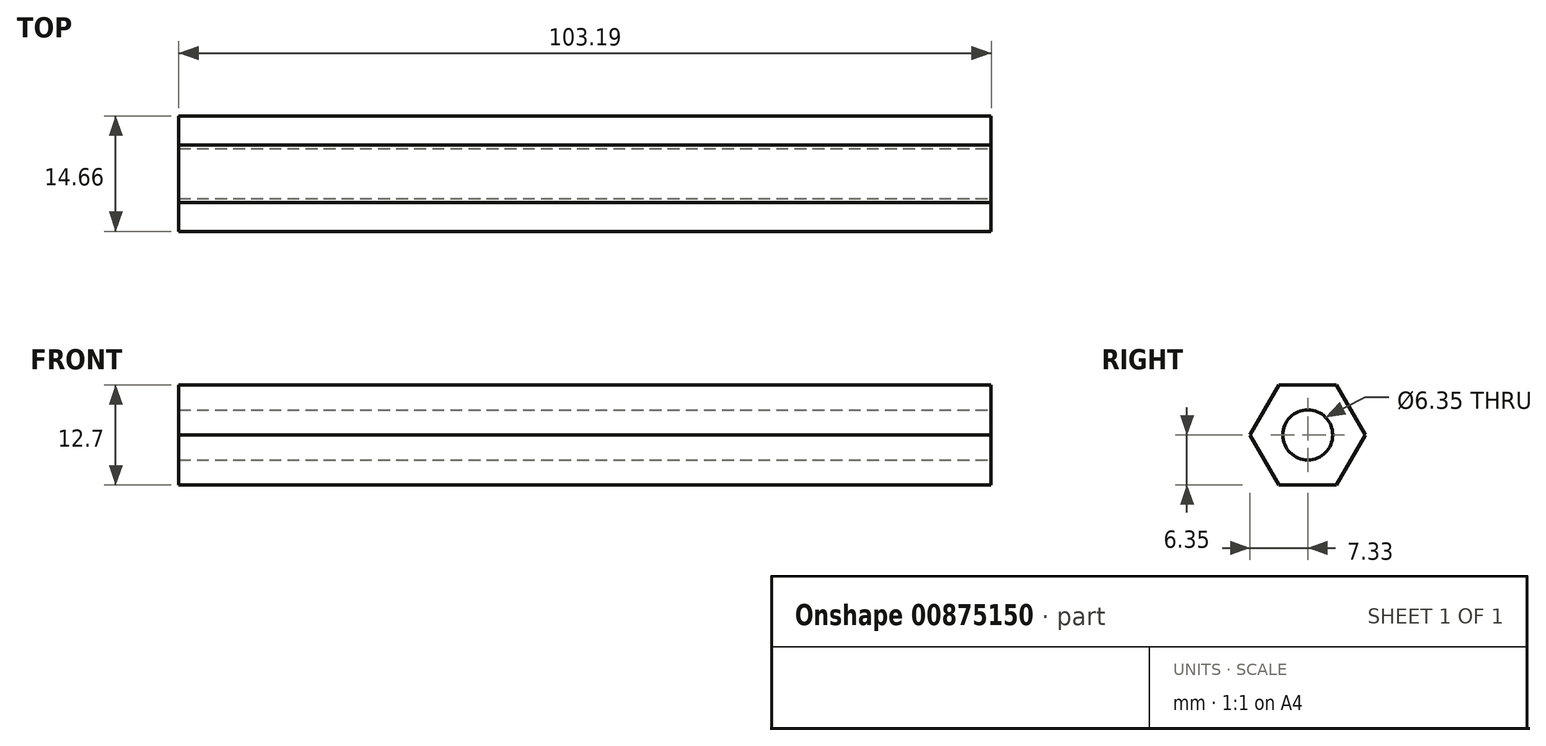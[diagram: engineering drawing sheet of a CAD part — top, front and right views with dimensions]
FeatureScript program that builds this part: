
annotation { "Feature Type Name" : "Feature", "Feature Type Description" : "" }
export const myFeature = defineFeature(function(context is Context, id is Id, definition is map)
    precondition{}
    {
        {
            var Q0;
            Q0=qCreatedBy(makeId("Right.planeOp"),FACE);
            var sketch = newSketch(context, id + "F0", { "sketchPlane" : qUnion([Q0])});
            skCircle(sketch, "E0.cCircle", {"center": v(0, 0) * mm, "radius": 6.35 * mm, "construction": true});
            skLineSegment(sketch, "E0.0", {"start": v(-3.67, 6.35) * mm, "end": v(3.67, 6.35) * mm});
            skLineSegment(sketch, "E0.1", {"start": v(3.67, 6.35) * mm, "end": v(7.33, 0) * mm});
            skLineSegment(sketch, "E0.2", {"start": v(7.33, 0) * mm, "end": v(3.67, -6.35) * mm});
            skLineSegment(sketch, "E0.3", {"start": v(3.67, -6.35) * mm, "end": v(-3.67, -6.35) * mm});
            skLineSegment(sketch, "E0.4", {"start": v(-3.67, -6.35) * mm, "end": v(-7.33, 0) * mm});
            skLineSegment(sketch, "E0.5", {"start": v(-7.33, 0) * mm, "end": v(-3.67, 6.35) * mm});
            skPoint(sketch, "E0.0.midPoint", {"position": v(0, 6.35) * mm});
            skSolve(sketch);
        }
        {
            var Q0;
            Q0 = qSketchRegion(id + "F0", true);
            extrude(context, id + "F1", {"entities" : qUnion([Q0]), "depth" : 103.19 * mm, "offsetDistance" : 25.4 * mm});
        }
        {
            var Q0;
            Q0=makeQuery(id+"F1.opExtrude","CAP_FACE",FACE,{"disambiguationData":[OSD([sQuery(id+"F0.wireOp",EDGE,"E0.0"),sQuery(id+"F0.wireOp",EDGE,"E0.1"),sQuery(id+"F0.wireOp",EDGE,"E0.2"),sQuery(id+"F0.wireOp",EDGE,"E0.3"),sQuery(id+"F0.wireOp",EDGE,"E0.4"),sQuery(id+"F0.wireOp",EDGE,"E0.5")])],"isStart":false});
            var sketch = newSketch(context, id + "F2", { "sketchPlane" : qUnion([Q0])});
            skCircle(sketch, "E1", {"center": v(0, 0) * mm, "radius": 3.18 * mm});
            skSolve(sketch);
        }
        {
            var Q0;
            Q0 = qSketchRegion(id + "F2", true);
            extrude(context, id + "F3", {"entities" : qUnion([Q0]), "operationType" : NewBodyOperationType.REMOVE, "endBound" : BoundingType.THROUGH_ALL, "oppositeDirection" : true, "depth" : 25.4 * mm, "offsetDistance" : 25.4 * mm});
        }
    });
